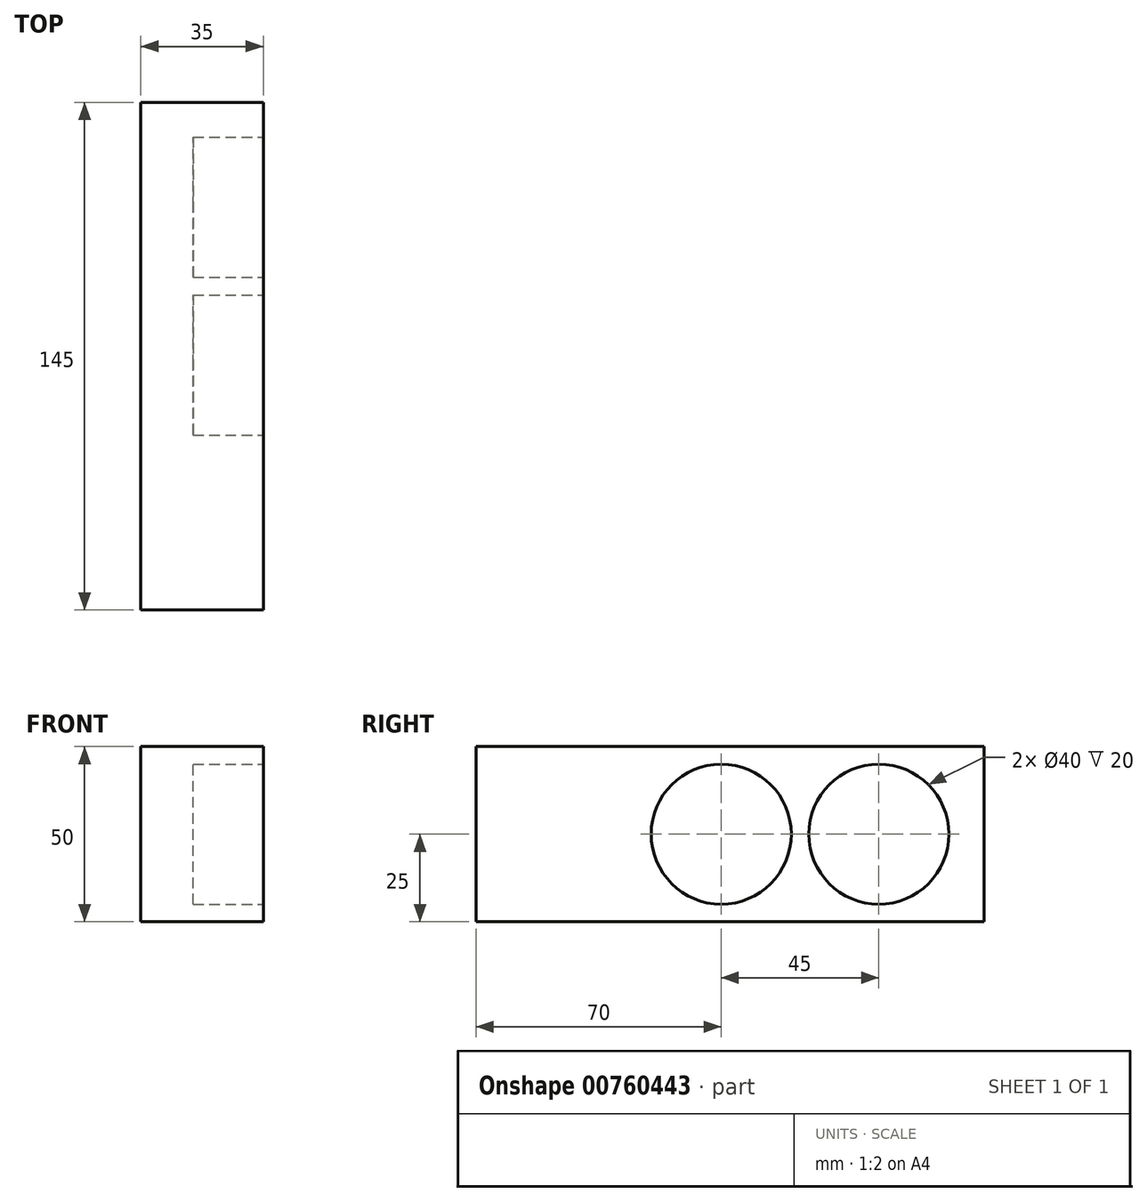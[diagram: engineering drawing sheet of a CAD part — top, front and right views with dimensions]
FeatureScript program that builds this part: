
annotation { "Feature Type Name" : "Feature", "Feature Type Description" : "" }
export const myFeature = defineFeature(function(context is Context, id is Id, definition is map)
    precondition{}
    {
        {
            var Q0;
            Q0=qCreatedBy(makeId("Front.planeOp"),FACE);
            var sketch = newSketch(context, id + "F0", { "sketchPlane" : qUnion([Q0])});
            skLineSegment(sketch, "E0.bottom", {"start": v(0, 0) * mm, "end": v(35, 0) * mm});
            skLineSegment(sketch, "E0.top", {"start": v(0, 50) * mm, "end": v(35, 50) * mm});
            skLineSegment(sketch, "E0.left", {"start": v(0, 0) * mm, "end": v(0, 50) * mm});
            skLineSegment(sketch, "E0.right", {"start": v(35, 0) * mm, "end": v(35, 50) * mm});
            skSolve(sketch);
        }
        {
            var Q0;
            Q0 = qSketchRegion(id + "F0", true);
            extrude(context, id + "F1", {"entities" : qUnion([Q0]), "depth" : 145 * mm, "offsetDistance" : 25 * mm});
        }
        {
            var Q0;
            Q0=makeQuery(id+"F1.opExtrude","SWEPT_FACE",FACE,{"disambiguationData":[OSD([sQuery(id+"F0.wireOp",EDGE,"E0.right")])]});
            var sketch = newSketch(context, id + "F2", { "sketchPlane" : qUnion([Q0])});
            skCircle(sketch, "E1", {"center": v(-75, 25) * mm, "radius": 20 * mm});
            skPoint(sketch, "E1.centerSnap0", {"position": v(-145, 25) * mm});
            skCircle(sketch, "E2", {"center": v(-30, 25) * mm, "radius": 20 * mm});
            skSolve(sketch);
        }
        {
            var Q0;
            Q0 = qSketchRegion(id + "F2", true);
            extrude(context, id + "F3", {"entities" : qUnion([Q0]), "operationType" : NewBodyOperationType.REMOVE, "oppositeDirection" : true, "depth" : 20 * mm, "offsetDistance" : 25 * mm});
        }
    });
